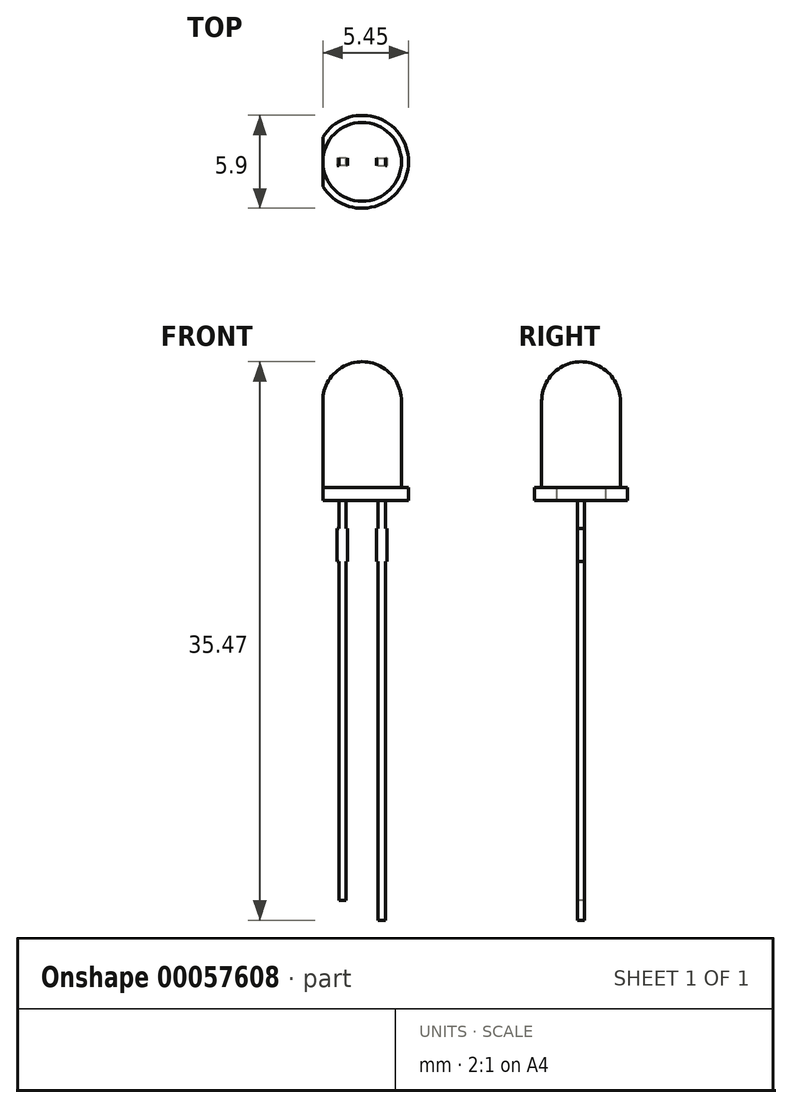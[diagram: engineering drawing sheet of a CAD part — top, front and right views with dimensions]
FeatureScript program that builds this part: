
annotation { "Feature Type Name" : "Feature", "Feature Type Description" : "" }
export const myFeature = defineFeature(function(context is Context, id is Id, definition is map)
    precondition{}
    {
        {
            var Q0;
            Q0=qCreatedBy(makeId("Top.planeOp"),FACE);
            var sketch = newSketch(context, id + "F0", { "sketchPlane" : qUnion([Q0])});
            skCircle(sketch, "E0", {"center": v(0, 0) * mm, "radius": 2.5 * mm});
            skCircle(sketch, "E1", {"center": v(0, 0) * mm, "radius": 2.95 * mm});
            skSolve(sketch);
        }
        {
            var Q0;
            Q0=makeQuery(id+"F0.imprint","IMPRINT",FACE,{"disambiguationData":[TD([[makeQuery(id+"F0.imprint","IMPRINT",EDGE,{"derivedFrom":sQuery(id+"F0.wireOp",EDGE,"E0")}),1.0]])]});
            extrude(context, id + "F1", {"entities" : qUnion([Q0]), "depth" : 8.8 * mm});
        }
        {
            var Q0;
            Q0=makeQuery(id+"F0.imprint","IMPRINT",FACE,{"disambiguationData":[TD([[makeQuery(id+"F0.imprint","IMPRINT",EDGE,{"derivedFrom":sQuery(id+"F0.wireOp",EDGE,"E0")}),-1.0]])]});
            extrude(context, id + "F2", {"entities" : qUnion([Q0]), "operationType" : NewBodyOperationType.ADD, "depth" : .8 * mm});
        }
        {
            var Q0;
            Q0=makeQuery(id+"F1.opExtrude","CAP_EDGE",EDGE,{"disambiguationData":[OSD([sQuery(id+"F0.wireOp",EDGE,"E0")])],"isStart":false});
            fillet(context, id + "F3", {"entities" : qUnion([Q0]), "radius" : 2.5 * mm, "tangentPropagation" : true, "allowEdgeOverflow" : false});
        }
        {
            var Q0;
            {var subQ0=sQuery(id+"F0.wireOp",EDGE,"E0");Q0=makeQuery(id+"F2.boolean.opBoolean","MERGE",FACE,{"derivedFrom":[makeQuery(id+"F1.opExtrude","CAP_FACE",FACE,{"disambiguationData":[OSD([subQ0])],"isStart":true}),makeQuery(id+"F2.opExtrude","CAP_FACE",FACE,{"disambiguationData":[OSD([subQ0,sQuery(id+"F0.wireOp",EDGE,"E1")])],"isStart":true})]});}
            var sketch = newSketch(context, id + "F4", { "sketchPlane" : qUnion([Q0])});
            skLineSegment(sketch, "E2", {"start": v(-2.5, 0) * mm, "end": v(-2.5, 1.57) * mm});
            skLineSegment(sketch, "E3", {"start": v(-2.5, 0) * mm, "end": v(-2.5, -1.57) * mm});
            skLineSegment(sketch, "E4.bottom", {"start": v(-1.02, -0.23) * mm, "end": v(-1.48, -0.23) * mm});
            skLineSegment(sketch, "E4.top", {"start": v(-1.02, 0.23) * mm, "end": v(-1.48, 0.23) * mm});
            skLineSegment(sketch, "E4.left", {"start": v(-1.02, -0.23) * mm, "end": v(-1.02, 0.23) * mm});
            skLineSegment(sketch, "E4.right", {"start": v(-1.48, -0.23) * mm, "end": v(-1.48, 0.23) * mm});
            skPoint(sketch, "E4.middle", {"position": v(-1.25, 0) * mm});
            skLineSegment(sketch, "E5.MirrorCS", {"start": v(1.48, -0.23) * mm, "end": v(1.48, 0.23) * mm});
            skLineSegment(sketch, "E6.MirrorCS", {"start": v(1.02, -0.23) * mm, "end": v(1.02, 0.23) * mm});
            skLineSegment(sketch, "E7.MirrorCS", {"start": v(1.02, 0.23) * mm, "end": v(1.48, 0.23) * mm});
            skLineSegment(sketch, "E8.MirrorCS", {"start": v(1.02, -0.23) * mm, "end": v(1.48, -0.23) * mm});
            skSolve(sketch);
        }
        {
            var Q0;
            {var subQ0=sQuery(id+"F4.wireOp",EDGE,"E2");Q0=makeQuery(id+"F4.imprint","IMPRINT",FACE,{"disambiguationData":[TD([[makeQuery(id+"F4.imprint","IMPRINT",EDGE,{"derivedFrom":subQ0}),1.0]])]});}
            extrude(context, id + "F5", {"entities" : qUnion([Q0]), "operationType" : NewBodyOperationType.REMOVE, "endBound" : BoundingType.UP_TO_NEXT, "oppositeDirection" : true, "depth" : 25 * mm});
        }
        {
            var Q0;
            Q0=makeQuery(id+"F4.imprint","IMPRINT",FACE,{"disambiguationData":[TD([[makeQuery(id+"F4.imprint","IMPRINT",EDGE,{"derivedFrom":sQuery(id+"F4.wireOp",EDGE,"E4.bottom")}),-1.0]])]});
            extrude(context, id + "F6", {"entities" : qUnion([Q0]), "depth" : 25.4 * mm});
        }
        {
            var Q0;
            Q0=makeQuery(id+"F6.opExtrude","SWEPT_FACE",FACE,{"disambiguationData":[OSD([sQuery(id+"F4.wireOp",EDGE,"E4.right")])]});
            var sketch = newSketch(context, id + "F7", { "sketchPlane" : qUnion([Q0])});
            skLineSegment(sketch, "E9.bottom", {"start": v(-0.23, -3.9) * mm, "end": v(0.23, -3.9) * mm});
            skLineSegment(sketch, "E9.top", {"start": v(-0.23, -1.8) * mm, "end": v(0.23, -1.8) * mm});
            skLineSegment(sketch, "E9.left", {"start": v(-0.23, -3.9) * mm, "end": v(-0.23, -1.8) * mm});
            skLineSegment(sketch, "E9.right", {"start": v(0.23, -3.9) * mm, "end": v(0.23, -1.8) * mm});
            skPoint(sketch, "E9.middle", {"position": v(0, -2.85) * mm});
            skSolve(sketch);
        }
        {
            var Q0;
            Q0 = qSketchRegion(id + "F7", true);
            extrude(context, id + "F8", {"entities" : qUnion([Q0]), "operationType" : NewBodyOperationType.ADD, "depth" : .1 * mm, "hasSecondDirection" : true, "secondDirectionOppositeDirection" : true, "secondDirectionDepth" : .56 * mm});
        }
        {
            var Q0;
            Q0=makeQuery(id+"F6.opExtrude","SWEPT_BODY",BODY,{"disambiguationData":[OSD([sQuery(id+"F4.wireOp",EDGE,"E4.bottom"),sQuery(id+"F4.wireOp",EDGE,"E4.top"),sQuery(id+"F4.wireOp",EDGE,"E4.left"),sQuery(id+"F4.wireOp",EDGE,"E4.right")])]});
            var Q1;
            Q1=qCreatedBy(makeId("Right.planeOp"),FACE);
            mirror(context, id + "F9", {"entities" : qUnion([Q0]), "mirrorPlane" : qUnion([Q1])});
        }
        {
            var Q0;
            Q0=makeQuery(id+"F9.opPattern","COPY",FACE,{"derivedFrom":makeQuery(id+"F6.opExtrude","CAP_FACE",FACE,{"disambiguationData":[OSD([sQuery(id+"F4.wireOp",EDGE,"E4.bottom"),sQuery(id+"F4.wireOp",EDGE,"E4.top"),sQuery(id+"F4.wireOp",EDGE,"E4.left"),sQuery(id+"F4.wireOp",EDGE,"E4.right")])],"isStart":false}),"instanceName":"1"});
            extrude(context, id + "F10", {"entities" : qUnion([Q0]), "operationType" : NewBodyOperationType.ADD, "depth" : 1.27 * mm});
        }
    });
